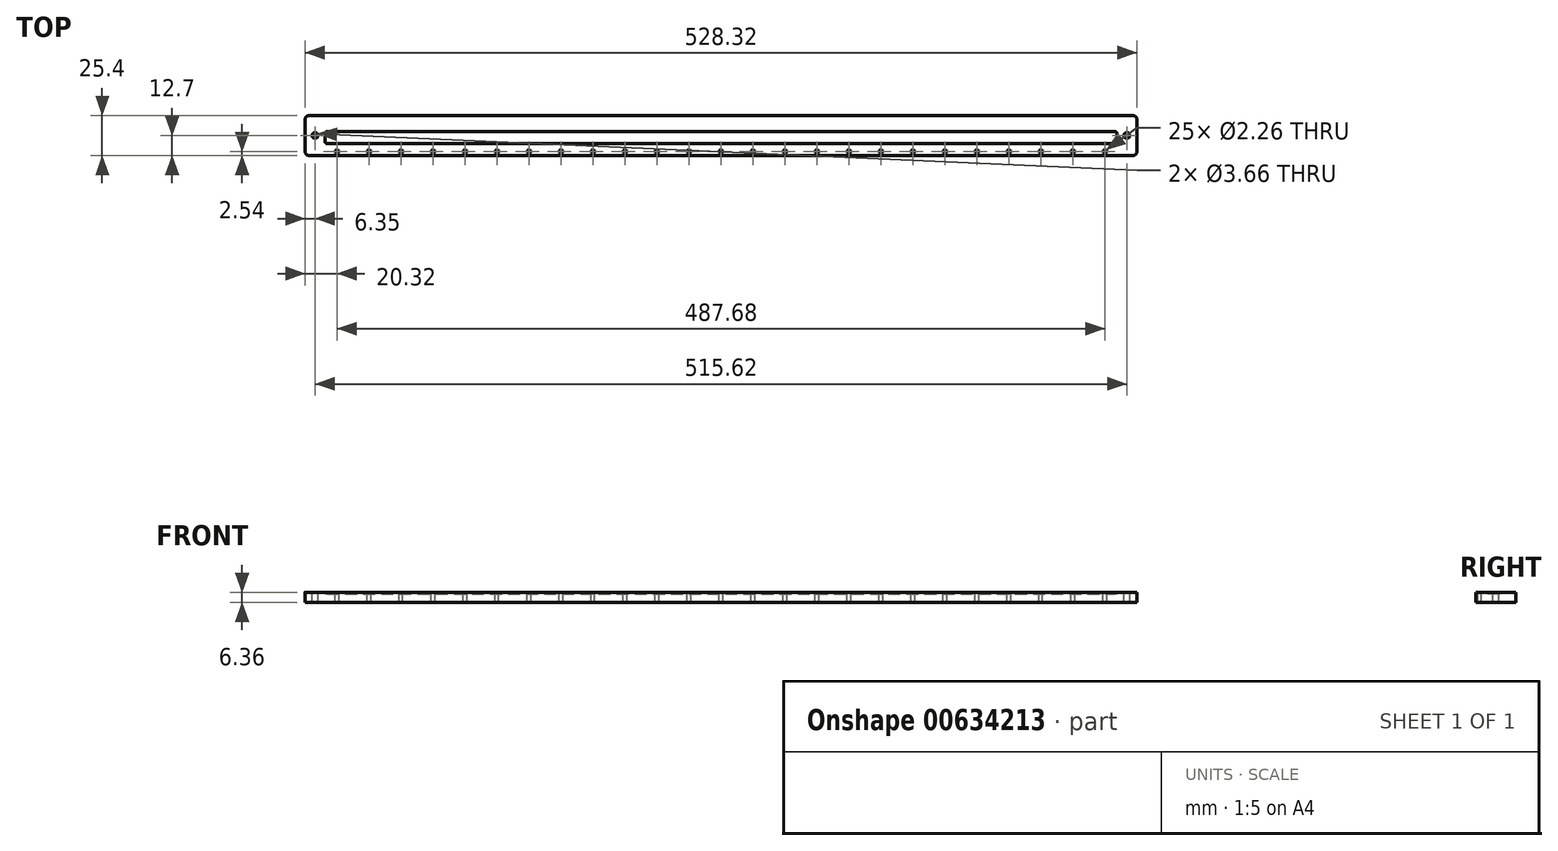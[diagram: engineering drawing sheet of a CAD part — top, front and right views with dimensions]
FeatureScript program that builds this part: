
annotation { "Feature Type Name" : "Feature", "Feature Type Description" : "" }
export const myFeature = defineFeature(function(context is Context, id is Id, definition is map)
    precondition{}
    {
        {
            var Q0;
            Q0=qCreatedBy(makeId("Top.planeOp"),FACE);
            var sketch = newSketch(context, id + "F0", { "sketchPlane" : qUnion([Q0])});
            skLineSegment(sketch, "E0.bottom", {"start": v(-264.16, 12.7) * mm, "end": v(264.16, 12.7) * mm});
            skLineSegment(sketch, "E0.top", {"start": v(-264.16, -12.7) * mm, "end": v(264.16, -12.7) * mm});
            skLineSegment(sketch, "E0.left", {"start": v(-264.16, 12.7) * mm, "end": v(-264.16, -12.7) * mm});
            skLineSegment(sketch, "E0.right", {"start": v(264.16, 12.7) * mm, "end": v(264.16, -12.7) * mm});
            skLineSegment(sketch, "E1", {"start": v(-264.16, -12.7) * mm, "end": v(264.16, 12.7) * mm, "construction": true});
            skSolve(sketch);
        }
        {
            var Q0;
            Q0 = qSketchRegion(id + "F0", true);
            extrude(context, id + "F1", {"entities" : qUnion([Q0]), "endBound" : BoundingType.SYMMETRIC, "depth" : 6.35 * mm, "offsetDistance" : 25.4 * mm});
        }
        {
            var Q0;
            Q0=makeQuery(id+"F1.opExtrude","CAP_FACE",FACE,{"disambiguationData":[OSD([sQuery(id+"F0.wireOp",EDGE,"E0.bottom"),sQuery(id+"F0.wireOp",EDGE,"E0.top"),sQuery(id+"F0.wireOp",EDGE,"E0.left"),sQuery(id+"F0.wireOp",EDGE,"E0.right")])],"isStart":false});
            var sketch = newSketch(context, id + "F2", { "sketchPlane" : qUnion([Q0])});
            skLineSegment(sketch, "E2.bottom", {"start": v(-251.46, 2.54) * mm, "end": v(251.46, 2.54) * mm});
            skLineSegment(sketch, "E2.top", {"start": v(-251.46, -5.08) * mm, "end": v(251.46, -5.08) * mm});
            skLineSegment(sketch, "E2.left", {"start": v(-251.46, 2.54) * mm, "end": v(-251.46, -5.08) * mm});
            skLineSegment(sketch, "E2.right", {"start": v(251.46, 2.54) * mm, "end": v(251.46, -5.08) * mm});
            skSolve(sketch);
        }
        {
            var Q0;
            Q0 = qSketchRegion(id + "F2", true);
            extrude(context, id + "F3", {"entities" : qUnion([Q0]), "operationType" : NewBodyOperationType.REMOVE, "oppositeDirection" : true, "depth" : 1.02 * mm, "offsetDistance" : 25.4 * mm});
        }
        {
            var Q0;
            Q0=makeQuery(id+"F1.opExtrude","CAP_FACE",FACE,{"disambiguationData":[OSD([sQuery(id+"F0.wireOp",EDGE,"E0.bottom"),sQuery(id+"F0.wireOp",EDGE,"E0.top"),sQuery(id+"F0.wireOp",EDGE,"E0.left"),sQuery(id+"F0.wireOp",EDGE,"E0.right")])],"isStart":false});
            var sketch = newSketch(context, id + "F4", { "sketchPlane" : qUnion([Q0])});
            skCircle(sketch, "E3", {"center": v(-257.81, 0) * mm, "radius": 1.83 * mm});
            skLineSegment(sketch, "E4", {"start": v(0, 12.7) * mm, "end": v(0, -12.7) * mm});
            skCircle(sketch, "E5.MirrorC", {"center": v(257.81, 0) * mm, "radius": 1.83 * mm});
            skSolve(sketch);
        }
        {
            var Q0;
            Q0 = qSketchRegion(id + "F4", true);
            extrude(context, id + "F5", {"entities" : qUnion([Q0]), "operationType" : NewBodyOperationType.REMOVE, "endBound" : BoundingType.THROUGH_ALL, "oppositeDirection" : true, "depth" : 25.4 * mm, "offsetDistance" : 25.4 * mm});
        }
        {
            var Q0;
            Q0=makeQuery(id+"F1.opExtrude","CAP_FACE",FACE,{"disambiguationData":[OSD([sQuery(id+"F0.wireOp",EDGE,"E0.bottom"),sQuery(id+"F0.wireOp",EDGE,"E0.top"),sQuery(id+"F0.wireOp",EDGE,"E0.left"),sQuery(id+"F0.wireOp",EDGE,"E0.right")])],"isStart":false});
            var sketch = newSketch(context, id + "F6", { "sketchPlane" : qUnion([Q0])});
            skPoint(sketch, "E6", {"position": v(-243.84, -10.16) * mm});
            skPoint(sketch, "E7.1.0.0", {"position": v(-223.52, -10.16) * mm});
            skPoint(sketch, "E7.2.0.0", {"position": v(-203.2, -10.16) * mm});
            skPoint(sketch, "E7.3.0.0", {"position": v(-182.88, -10.16) * mm});
            skPoint(sketch, "E7.4.0.0", {"position": v(-162.56, -10.16) * mm});
            skPoint(sketch, "E7.5.0.0", {"position": v(-142.24, -10.16) * mm});
            skPoint(sketch, "E7.6.0.0", {"position": v(-121.92, -10.16) * mm});
            skPoint(sketch, "E7.7.0.0", {"position": v(-101.6, -10.16) * mm});
            skPoint(sketch, "E7.8.0.0", {"position": v(-81.28, -10.16) * mm});
            skPoint(sketch, "E7.9.0.0", {"position": v(-60.96, -10.16) * mm});
            skPoint(sketch, "E7.10.0.0", {"position": v(-40.64, -10.16) * mm});
            skPoint(sketch, "E7.11.0.0", {"position": v(-20.32, -10.16) * mm});
            skPoint(sketch, "E7.12.0.0", {"position": v(0, -10.16) * mm});
            skPoint(sketch, "E7.13.0.0", {"position": v(20.32, -10.16) * mm});
            skPoint(sketch, "E7.14.0.0", {"position": v(40.64, -10.16) * mm});
            skPoint(sketch, "E7.15.0.0", {"position": v(60.96, -10.16) * mm});
            skPoint(sketch, "E7.16.0.0", {"position": v(81.28, -10.16) * mm});
            skPoint(sketch, "E7.17.0.0", {"position": v(101.6, -10.16) * mm});
            skPoint(sketch, "E7.18.0.0", {"position": v(121.92, -10.16) * mm});
            skPoint(sketch, "E7.19.0.0", {"position": v(142.24, -10.16) * mm});
            skPoint(sketch, "E7.20.0.0", {"position": v(162.56, -10.16) * mm});
            skPoint(sketch, "E7.21.0.0", {"position": v(182.88, -10.16) * mm});
            skPoint(sketch, "E7.22.0.0", {"position": v(203.2, -10.16) * mm});
            skPoint(sketch, "E7.23.0.0", {"position": v(223.52, -10.16) * mm});
            skPoint(sketch, "E7.24.0.0", {"position": v(243.84, -10.16) * mm});
            skLineSegment(sketch, "E7.direction1", {"start": v(-243.84, -10.16) * mm, "end": v(-223.52, -10.16) * mm, "construction": true});
            skSolve(sketch);
        }
        {
            var Q0;
            Q0=sQuery(id+"F6.wireOp",VERTEX,"E7.9.0.0");
            var Q1;
            Q1=sQuery(id+"F6.wireOp",VERTEX,"E7.10.0.0");
            var Q2;
            Q2=sQuery(id+"F6.wireOp",VERTEX,"E7.21.0.0");
            var Q3;
            Q3=sQuery(id+"F6.wireOp",VERTEX,"E7.6.0.0");
            var Q4;
            Q4=sQuery(id+"F6.wireOp",VERTEX,"E7.8.0.0");
            var Q5;
            Q5=sQuery(id+"F6.wireOp",VERTEX,"E7.7.0.0");
            var Q6;
            Q6=sQuery(id+"F6.wireOp",VERTEX,"E7.22.0.0");
            var Q7;
            Q7=sQuery(id+"F6.wireOp",VERTEX,"E7.15.0.0");
            var Q8;
            Q8=sQuery(id+"F6.wireOp",VERTEX,"E7.14.0.0");
            var Q9;
            Q9=sQuery(id+"F6.wireOp",VERTEX,"E7.24.0.0");
            var Q10;
            Q10=sQuery(id+"F6.wireOp",VERTEX,"E7.23.0.0");
            var Q11;
            Q11=sQuery(id+"F6.wireOp",VERTEX,"E7.11.0.0");
            var Q12;
            Q12=sQuery(id+"F6.wireOp",VERTEX,"E7.20.0.0");
            var Q13;
            Q13=sQuery(id+"F6.wireOp",VERTEX,"E7.12.0.0");
            var Q14;
            Q14=sQuery(id+"F6.wireOp",VERTEX,"E7.13.0.0");
            var Q15;
            Q15=sQuery(id+"F6.wireOp",VERTEX,"E7.19.0.0");
            var Q16;
            Q16=sQuery(id+"F6.wireOp",VERTEX,"E7.18.0.0");
            var Q17;
            Q17=sQuery(id+"F6.wireOp",VERTEX,"E7.17.0.0");
            var Q18;
            Q18=sQuery(id+"F6.wireOp",VERTEX,"E7.16.0.0");
            var Q19;
            Q19=sQuery(id+"F6.wireOp",VERTEX,"E6");
            var Q20;
            Q20=sQuery(id+"F6.wireOp",VERTEX,"E7.1.0.0");
            var Q21;
            Q21=sQuery(id+"F6.wireOp",VERTEX,"E7.2.0.0");
            var Q22;
            Q22=sQuery(id+"F6.wireOp",VERTEX,"E7.3.0.0");
            var Q23;
            Q23=sQuery(id+"F6.wireOp",VERTEX,"E7.4.0.0");
            var Q24;
            Q24=sQuery(id+"F6.wireOp",VERTEX,"E7.5.0.0");
            var Q25;
            Q25=makeQuery(id+"F1.opExtrude","SWEPT_BODY",BODY,{"disambiguationData":[OSD([sQuery(id+"F0.wireOp",EDGE,"E0.bottom"),sQuery(id+"F0.wireOp",EDGE,"E0.top"),sQuery(id+"F0.wireOp",EDGE,"E0.left"),sQuery(id+"F0.wireOp",EDGE,"E0.right")])]});
            hole(context, id + "F7", {"style" : HoleStyle.SIMPLE, "endStyle" : HoleEndStyle.THROUGH, "standardTappedOrClearance" : lookupTablePath({ "standard" : "ANSI", "engagement" : "75%", "pitch" : "40 tpi", "size" : "#4", "type" : "Tapped" }), "standardBlindInLast" : lookupTablePath({ "standard" : "ANSI", "engagement" : "75%", "pitch" : "40 tpi", "size" : "#4", "type" : "Tapped" }), "holeDiameter" : 2.26 * mm, "majorDiameter" : 2.84 * mm, "showTappedDepth" : true, "isTappedThrough" : true, "tappedDepth" : 12.7 * mm, "tapClearance" : 3, "locations" : qUnion([Q0, Q1, Q2, Q3, Q4, Q5, Q6, Q7, Q8, Q9, Q10, Q11, Q12, Q13, Q14, Q15, Q16, Q17, Q18, Q19, Q20, Q21, Q22, Q23, Q24]), "scope" : qUnion([Q25])});
        }
        {
            var Q0;
            Q0=makeQuery(id+"F1.opExtrude","SWEPT_EDGE",EDGE,{"disambiguationData":[OSD([sQuery(id+"F0.wireOp",EDGE,"E0.top"),sQuery(id+"F0.wireOp",EDGE,"E0.right")])]});
            var Q1;
            Q1=makeQuery(id+"F1.opExtrude","SWEPT_EDGE",EDGE,{"disambiguationData":[OSD([sQuery(id+"F0.wireOp",EDGE,"E0.bottom"),sQuery(id+"F0.wireOp",EDGE,"E0.right")])]});
            var Q2;
            Q2=makeQuery(id+"F1.opExtrude","SWEPT_EDGE",EDGE,{"disambiguationData":[OSD([sQuery(id+"F0.wireOp",EDGE,"E0.top"),sQuery(id+"F0.wireOp",EDGE,"E0.left")])]});
            var Q3;
            Q3=makeQuery(id+"F1.opExtrude","SWEPT_EDGE",EDGE,{"disambiguationData":[OSD([sQuery(id+"F0.wireOp",EDGE,"E0.bottom"),sQuery(id+"F0.wireOp",EDGE,"E0.left")])]});
            fillet(context, id + "F8", {"entities" : qUnion([Q0, Q1, Q2, Q3]), "radius" : 2.54 * mm, "tangentPropagation" : true, "allowEdgeOverflow" : false});
        }
        {
            var Q0;
            Q0=makeQuery(id+"F3.boolean.opBoolean","COPY",EDGE,{"derivedFrom":makeQuery(id+"F3.opExtrude","SWEPT_EDGE",EDGE,{"disambiguationData":[OSD([sQuery(id+"F2.wireOp",EDGE,"E2.top"),sQuery(id+"F2.wireOp",EDGE,"E2.left")])]})});
            var Q1;
            Q1=makeQuery(id+"F3.boolean.opBoolean","COPY",EDGE,{"derivedFrom":makeQuery(id+"F3.opExtrude","SWEPT_EDGE",EDGE,{"disambiguationData":[OSD([sQuery(id+"F2.wireOp",EDGE,"E2.bottom"),sQuery(id+"F2.wireOp",EDGE,"E2.left")])]})});
            var Q2;
            Q2=makeQuery(id+"F3.boolean.opBoolean","COPY",EDGE,{"derivedFrom":makeQuery(id+"F3.opExtrude","SWEPT_EDGE",EDGE,{"disambiguationData":[OSD([sQuery(id+"F2.wireOp",EDGE,"E2.top"),sQuery(id+"F2.wireOp",EDGE,"E2.right")])]})});
            var Q3;
            Q3=makeQuery(id+"F3.boolean.opBoolean","COPY",EDGE,{"derivedFrom":makeQuery(id+"F3.opExtrude","SWEPT_EDGE",EDGE,{"disambiguationData":[OSD([sQuery(id+"F2.wireOp",EDGE,"E2.bottom"),sQuery(id+"F2.wireOp",EDGE,"E2.right")])]})});
            fillet(context, id + "F9", {"entities" : qUnion([Q0, Q1, Q2, Q3]), "radius" : 1.27 * mm, "tangentPropagation" : true, "allowEdgeOverflow" : false});
        }
    });
